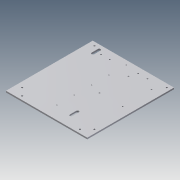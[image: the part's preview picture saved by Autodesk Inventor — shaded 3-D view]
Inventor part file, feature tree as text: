
AUTODESK INVENTOR PART (.ipt)
format: ipt  version: 2014 (Build 180170000, 170)  size: 180,224 bytes
history: native  units: mm
features: extrude x4, sketch x4
ambient origin geometry x8: Origin, YZ Plane, XZ Plane, XY Plane, X Axis, Y Axis, Z Axis, Center Point
bodies: Solid1 (feature_tree)
feature tree (8):
  extrude  "Extrusion1"  Depth=281.0mm
  extrude  "Extrusion5"  Depth=5.0mm
  extrude  "Extrusion6"  Depth=12.5mm
  extrude  "Extrusion7"  Depth=10.0mm
  sketch  "Sketch1"  dims[d0=300.0mm d1=281.0mm]
  sketch  "Sketch5"  dims[d2=5.0mm d3=0.0mm d33=18.5mm d34=18.5mm]
  sketch  "Sketch6"  dims[d35=37.5mm d36=12.5mm]
  sketch  "Sketch7"  dims[d37=5.4mm d38=12.5mm d39=37.5mm d40=43.5mm d41=10.0mm d42=0.0mm d43=250.0mm d44=15.0mm d45=60.0mm d46=3.2mm d47=6.0mm d48=25.0mm d49=40.0mm d50=10.0mm d51=0.0mm d52=50.0mm d53=51.0mm d54=25.0mm d55=54.0mm d56=50.0mm d57=30.0mm d58=4.4mm d59=10.0mm d60=27.0mm d61=37.5mm d62=22.0mm d63=9.0mm d64=3.0mm d65=60.0mm d66=3.0mm d67=15.5mm d68=31.75mm d69=42.8625mm d70=5.55625mm d71=25.003125mm d72=5.55625mm d73=4.572mm d74=35.0mm d75=40.0mm d76=100.0mm d77=80.0mm d78=4.4mm d79=20.0mm d80=20.0mm d81=10.0mm d82=0.0mm d83=12.5mm d84=72.69375mm d85=19.446875mm]
